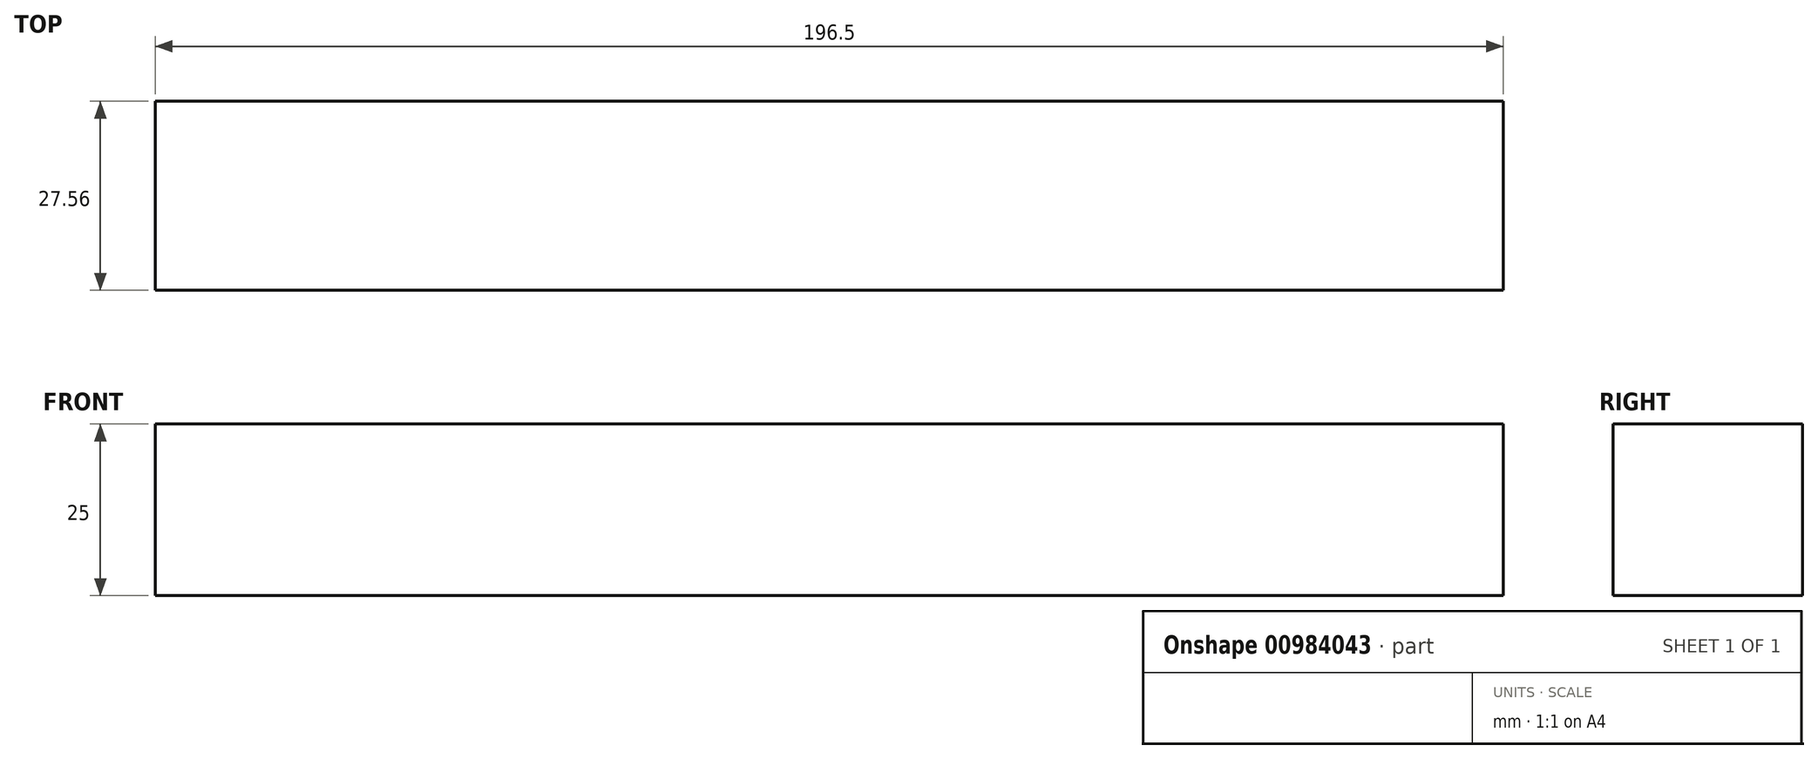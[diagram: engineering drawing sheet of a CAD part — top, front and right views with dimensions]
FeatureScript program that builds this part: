
annotation { "Feature Type Name" : "Feature", "Feature Type Description" : "" }
export const myFeature = defineFeature(function(context is Context, id is Id, definition is map)
    precondition{}
    {
        {
            var Q0;
            Q0=qCreatedBy(makeId("Top.planeOp"),FACE);
            var sketch = newSketch(context, id + "F0", { "sketchPlane" : qUnion([Q0])});
            skLineSegment(sketch, "E0.bottom", {"start": v(-98.25, -13.78) * mm, "end": v(98.25, -13.78) * mm});
            skLineSegment(sketch, "E0.top", {"start": v(-98.25, 13.78) * mm, "end": v(98.25, 13.78) * mm});
            skLineSegment(sketch, "E0.left", {"start": v(-98.25, -13.78) * mm, "end": v(-98.25, 13.78) * mm});
            skLineSegment(sketch, "E0.right", {"start": v(98.25, -13.78) * mm, "end": v(98.25, 13.78) * mm});
            skPoint(sketch, "E0.middle", {"position": v(0, 0) * mm});
            skSolve(sketch);
        }
        {
            var Q0;
            Q0=makeQuery(id+"F0.imprint","IMPRINT",FACE,{"disambiguationData":[TD([[makeQuery(id+"F0.imprint","IMPRINT",EDGE,{"derivedFrom":sQuery(id+"F0.wireOp",EDGE,"E0.bottom")}),1.0]])]});
            var sketch = newSketch(context, id + "F1", { "sketchPlane" : qUnion([Q0])});
            skSolve(sketch);
        }
        {
            var Q0;
            Q0=makeQuery(id+"F1.imprint","IMPRINT",FACE,{"disambiguationData":[TD([[makeQuery(id+"F1.imprint","IMPRINT",EDGE,{"derivedFrom":makeQuery(id+"F0.imprint","IMPRINT",EDGE,{"derivedFrom":sQuery(id+"F0.wireOp",EDGE,"E0.bottom")})}),1.0]])]});
            extrude(context, id + "F2", {"entities" : qUnion([Q0]), "depth" : 25 * mm, "offsetDistance" : 25 * mm});
        }
    });
